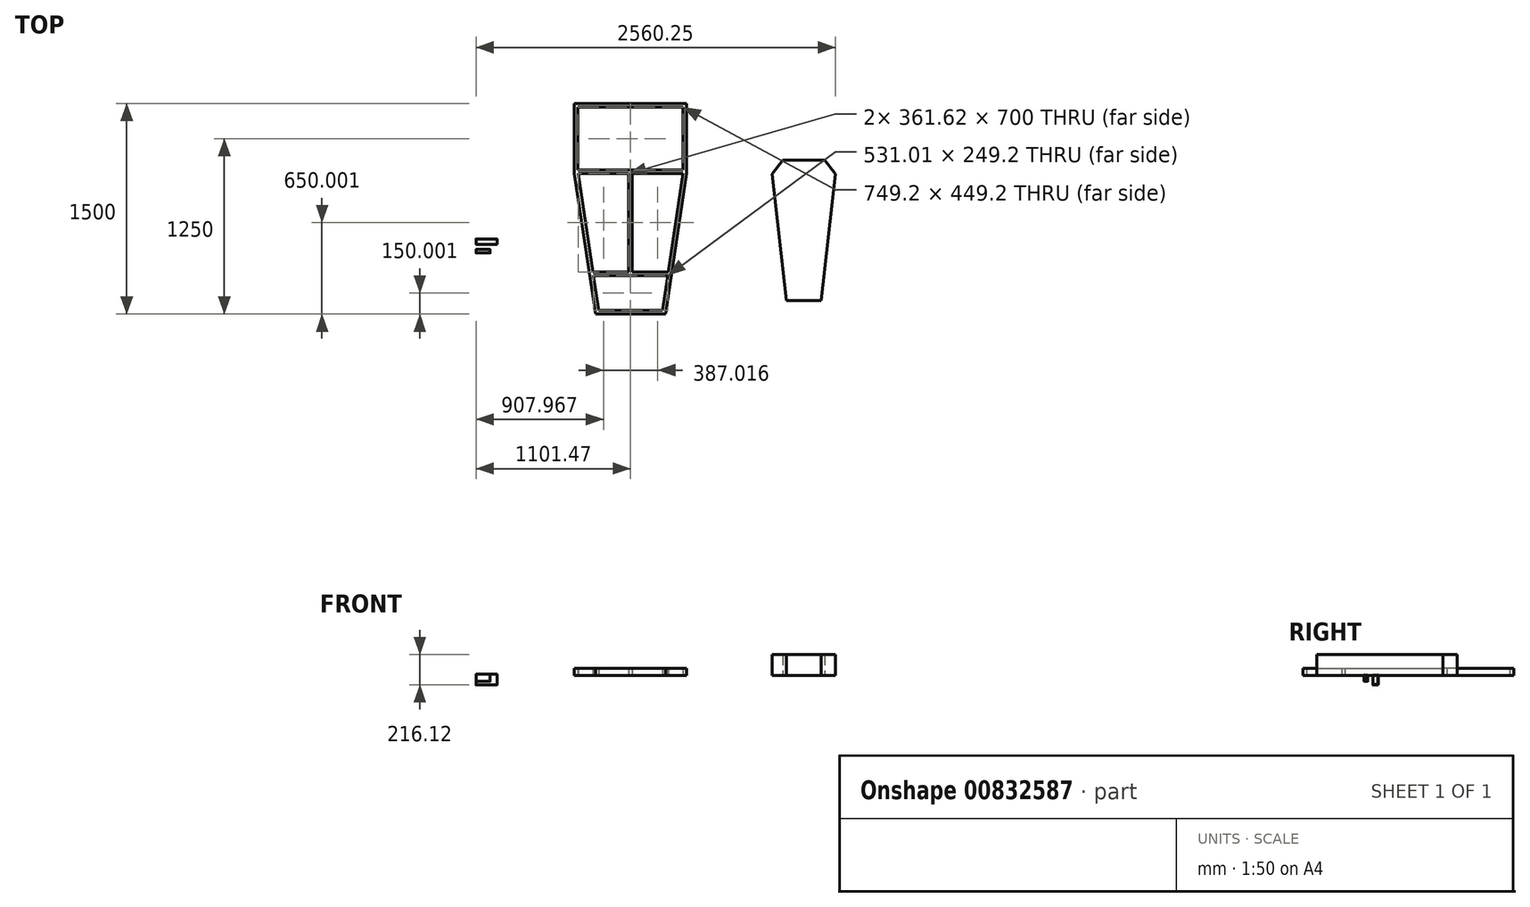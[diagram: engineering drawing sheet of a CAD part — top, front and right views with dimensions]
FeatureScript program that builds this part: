
annotation { "Feature Type Name" : "Feature", "Feature Type Description" : "" }
export const myFeature = defineFeature(function(context is Context, id is Id, definition is map)
    precondition{}
    {
        {
            var Q0;
            Q0=qCreatedBy(makeId("Right.planeOp"),FACE);
            var sketch = newSketch(context, id + "F0", { "sketchPlane" : qUnion([Q0])});
            skLineSegment(sketch, "E0.bottom", {"start": v(-5.09, 9.16) * mm, "end": v(18.31, 9.16) * mm});
            skLineSegment(sketch, "E0.top", {"start": v(-5.09, -41.64) * mm, "end": v(18.31, -41.64) * mm});
            skLineSegment(sketch, "E0.left", {"start": v(-6.09, 8.16) * mm, "end": v(-6.09, -40.64) * mm});
            skLineSegment(sketch, "E0.right", {"start": v(19.31, 8.16) * mm, "end": v(19.31, -40.64) * mm});
            skPoint(sketch, "E1.visualSharp", {"position": v(-6.09, 9.16) * mm});
            skArc(sketch, "E1.filletArc", {"start": v(-5.09, 9.16) * mm, "mid": v(-5.8, 8.87) * mm, "end": v(-6.09, 8.16) * mm});
            skPoint(sketch, "E2.visualSharp", {"position": v(19.31, 9.16) * mm});
            skArc(sketch, "E2.filletArc", {"start": v(19.31, 8.16) * mm, "mid": v(19.02, 8.87) * mm, "end": v(18.31, 9.16) * mm});
            skPoint(sketch, "E3.visualSharp", {"position": v(19.31, -41.64) * mm});
            skArc(sketch, "E3.filletArc", {"start": v(18.31, -41.64) * mm, "mid": v(19.02, -41.34) * mm, "end": v(19.31, -40.64) * mm});
            skPoint(sketch, "E4.visualSharp", {"position": v(-6.09, -41.64) * mm});
            skArc(sketch, "E4.filletArc", {"start": v(-6.09, -40.64) * mm, "mid": v(-5.8, -41.34) * mm, "end": v(-5.09, -41.64) * mm});
            skLineSegment(sketch, "E5.0", {"start": v(-2.98, 7.06) * mm, "end": v(16.2, 7.06) * mm});
            skLineSegment(sketch, "E5.1", {"start": v(-3.98, 6.06) * mm, "end": v(-3.98, -38.53) * mm});
            skLineSegment(sketch, "E5.2", {"start": v(-2.98, -39.53) * mm, "end": v(16.2, -39.53) * mm});
            skLineSegment(sketch, "E5.3", {"start": v(17.2, 6.06) * mm, "end": v(17.2, -38.53) * mm});
            skPoint(sketch, "E6.visualSharp", {"position": v(-3.98, 7.06) * mm});
            skArc(sketch, "E6.filletArc", {"start": v(-2.98, 7.06) * mm, "mid": v(-3.69, 6.76) * mm, "end": v(-3.98, 6.06) * mm});
            skPoint(sketch, "E7.visualSharp", {"position": v(17.2, 7.06) * mm});
            skArc(sketch, "E7.filletArc", {"start": v(17.2, 6.06) * mm, "mid": v(16.91, 6.76) * mm, "end": v(16.2, 7.06) * mm});
            skPoint(sketch, "E8.visualSharp", {"position": v(-3.98, -39.53) * mm});
            skArc(sketch, "E8.filletArc", {"start": v(-3.98, -38.53) * mm, "mid": v(-3.69, -39.24) * mm, "end": v(-2.98, -39.53) * mm});
            skPoint(sketch, "E9.visualSharp", {"position": v(17.2, -39.53) * mm});
            skArc(sketch, "E9.filletArc", {"start": v(16.2, -39.53) * mm, "mid": v(16.91, -39.24) * mm, "end": v(17.2, -38.53) * mm});
            skLineSegment(sketch, "E10.bottom", {"start": v(56.7, 10.08) * mm, "end": v(92.8, 10.08) * mm});
            skLineSegment(sketch, "E10.top", {"start": v(56.7, -66.12) * mm, "end": v(92.8, -66.12) * mm});
            skLineSegment(sketch, "E10.left", {"start": v(55.7, 9.08) * mm, "end": v(55.7, -65.12) * mm});
            skLineSegment(sketch, "E10.right", {"start": v(93.8, 9.08) * mm, "end": v(93.8, -65.12) * mm});
            skLineSegment(sketch, "E11.0", {"start": v(57.81, 6.97) * mm, "end": v(57.81, -63.01) * mm});
            skLineSegment(sketch, "E11.1", {"start": v(58.81, 7.97) * mm, "end": v(90.7, 7.97) * mm});
            skLineSegment(sketch, "E11.2", {"start": v(91.7, 6.97) * mm, "end": v(91.7, -63.01) * mm});
            skLineSegment(sketch, "E11.3", {"start": v(58.81, -64.01) * mm, "end": v(90.7, -64.01) * mm});
            skPoint(sketch, "E12.visualSharp", {"position": v(55.7, 10.08) * mm});
            skArc(sketch, "E12.filletArc", {"start": v(56.7, 10.08) * mm, "mid": v(56, 9.79) * mm, "end": v(55.7, 9.08) * mm});
            skPoint(sketch, "E13.visualSharp", {"position": v(57.81, 7.97) * mm});
            skArc(sketch, "E13.filletArc", {"start": v(58.81, 7.97) * mm, "mid": v(58.1, 7.68) * mm, "end": v(57.81, 6.97) * mm});
            skPoint(sketch, "E14.visualSharp", {"position": v(91.7, 7.97) * mm});
            skArc(sketch, "E14.filletArc", {"start": v(91.7, 6.97) * mm, "mid": v(91.4, 7.68) * mm, "end": v(90.7, 7.97) * mm});
            skPoint(sketch, "E15.visualSharp", {"position": v(93.8, 10.08) * mm});
            skArc(sketch, "E15.filletArc", {"start": v(93.8, 9.08) * mm, "mid": v(93.51, 9.79) * mm, "end": v(92.8, 10.08) * mm});
            skPoint(sketch, "E16.visualSharp", {"position": v(91.7, -64.01) * mm});
            skArc(sketch, "E16.filletArc", {"start": v(90.7, -64.01) * mm, "mid": v(91.4, -63.72) * mm, "end": v(91.7, -63.01) * mm});
            skPoint(sketch, "E17.visualSharp", {"position": v(93.8, -66.12) * mm});
            skArc(sketch, "E17.filletArc", {"start": v(92.8, -66.12) * mm, "mid": v(93.51, -65.83) * mm, "end": v(93.8, -65.12) * mm});
            skPoint(sketch, "E18.visualSharp", {"position": v(55.7, -66.12) * mm});
            skArc(sketch, "E18.filletArc", {"start": v(55.7, -65.12) * mm, "mid": v(56, -65.83) * mm, "end": v(56.7, -66.12) * mm});
            skPoint(sketch, "E19.visualSharp", {"position": v(57.81, -64.01) * mm});
            skArc(sketch, "E19.filletArc", {"start": v(57.81, -63.01) * mm, "mid": v(58.1, -63.72) * mm, "end": v(58.81, -64.01) * mm});
            skSolve(sketch);
        }
        {
            var Q0;
            Q0=makeQuery(id+"F0.imprint","IMPRINT",FACE,{"disambiguationData":[TD([[makeQuery(id+"F0.imprint","IMPRINT",EDGE,{"derivedFrom":sQuery(id+"F0.wireOp",EDGE,"E0.bottom")}),-1.0]])]});
            extrude(context, id + "F1", {"entities" : qUnion([Q0]), "depth" : 100 * mm, "offsetDistance" : 25 * mm});
        }
        {
            var Q0;
            Q0=makeQuery(id+"F0.imprint","IMPRINT",FACE,{"disambiguationData":[TD([[makeQuery(id+"F0.imprint","IMPRINT",EDGE,{"derivedFrom":sQuery(id+"F0.wireOp",EDGE,"E10.bottom")}),-1.0]])]});
            extrude(context, id + "F2", {"entities" : qUnion([Q0]), "depth" : 150 * mm, "offsetDistance" : 25 * mm});
        }
        {
            var Q0;
            Q0=qCreatedBy(makeId("Top.planeOp"),FACE);
            var sketch = newSketch(context, id + "F3", { "sketchPlane" : qUnion([Q0])});
            skLineSegment(sketch, "E20.left", {"start": v(701.47, 1058.38) * mm, "end": v(701.47, 558.38) * mm});
            skLineSegment(sketch, "E20.right", {"start": v(1501.47, 1058.38) * mm, "end": v(1501.47, 558.38) * mm});
            skLineSegment(sketch, "E21", {"start": v(701.47, 1058.38) * mm, "end": v(1501.47, 1058.38) * mm});
            skLineSegment(sketch, "E22", {"start": v(1114.17, 558.38) * mm, "end": v(1475.8, 558.38) * mm});
            skLineSegment(sketch, "E23", {"start": v(1088.77, 558.38) * mm, "end": v(727.16, 558.38) * mm});
            skLineSegment(sketch, "E24", {"start": v(1101.47, -441.62) * mm, "end": v(1351.47, -441.62) * mm});
            skLineSegment(sketch, "E25", {"start": v(1351.47, -441.62) * mm, "end": v(1501.47, 558.38) * mm});
            skLineSegment(sketch, "E26", {"start": v(1101.47, -441.62) * mm, "end": v(851.47, -441.62) * mm});
            skLineSegment(sketch, "E27", {"start": v(851.47, -441.62) * mm, "end": v(701.47, 558.38) * mm});
            skLineSegment(sketch, "E28.0", {"start": v(726.87, 1032.98) * mm, "end": v(726.87, 583.78) * mm});
            skLineSegment(sketch, "E28.1", {"start": v(873.35, -416.22) * mm, "end": v(835.97, -167.02) * mm});
            skLineSegment(sketch, "E28.2", {"start": v(1476.07, 1032.98) * mm, "end": v(1476.07, 583.78) * mm});
            skLineSegment(sketch, "E28.3", {"start": v(1329.6, -416.22) * mm, "end": v(1366.98, -167.02) * mm});
            skLineSegment(sketch, "E28.4", {"start": v(1101.47, -416.22) * mm, "end": v(1329.6, -416.22) * mm});
            skLineSegment(sketch, "E28.5", {"start": v(726.87, 1032.98) * mm, "end": v(1476.07, 1032.98) * mm});
            skLineSegment(sketch, "E28.6", {"start": v(1101.47, -416.22) * mm, "end": v(873.35, -416.22) * mm});
            skLineSegment(sketch, "E29.0", {"start": v(1101.47, 583.78) * mm, "end": v(726.87, 583.78) * mm});
            skLineSegment(sketch, "E29.1", {"start": v(1101.47, 583.78) * mm, "end": v(1476.07, 583.78) * mm});
            skLineSegment(sketch, "E30", {"start": v(1088.77, -141.62) * mm, "end": v(832.16, -141.62) * mm});
            skLineSegment(sketch, "E31", {"start": v(1114.17, -141.62) * mm, "end": v(1370.8, -141.62) * mm});
            skLineSegment(sketch, "E32.0", {"start": v(1114.17, -141.62) * mm, "end": v(1114.17, 558.38) * mm});
            skLineSegment(sketch, "E33.0", {"start": v(1088.77, -141.62) * mm, "end": v(1088.77, 558.38) * mm});
            skLineSegment(sketch, "E34.0", {"start": v(1101.47, -167.02) * mm, "end": v(835.97, -167.02) * mm});
            skLineSegment(sketch, "E34.1", {"start": v(1101.47, -167.02) * mm, "end": v(1366.98, -167.02) * mm});
            skLineSegment(sketch, "E35.trimOffspring", {"start": v(1370.8, -141.62) * mm, "end": v(1476.07, 560.28) * mm});
            skLineSegment(sketch, "E36.trimOffspring", {"start": v(832.16, -141.62) * mm, "end": v(726.87, 560.28) * mm});
            skSolve(sketch);
        }
        {
            var Q0;
            Q0=qCreatedBy(makeId("Top.planeOp"),FACE);
            var sketch = newSketch(context, id + "F4", { "sketchPlane" : qUnion([Q0])});
            skLineSegment(sketch, "E37", {"start": v(2335.25, -344.21) * mm, "end": v(2210.25, -344.21) * mm});
            skLineSegment(sketch, "E38", {"start": v(2335.25, -344.21) * mm, "end": v(2460.25, -344.21) * mm});
            skLineSegment(sketch, "E39", {"start": v(2560.25, 555.79) * mm, "end": v(2460.25, -344.21) * mm});
            skLineSegment(sketch, "E40", {"start": v(2110.25, 555.79) * mm, "end": v(2210.25, -344.21) * mm});
            skLineSegment(sketch, "E41", {"start": v(2335.25, 655.79) * mm, "end": v(2185.25, 655.79) * mm});
            skLineSegment(sketch, "E42", {"start": v(2185.25, 655.79) * mm, "end": v(2110.25, 555.79) * mm});
            skLineSegment(sketch, "E43", {"start": v(2335.25, 655.79) * mm, "end": v(2485.25, 655.79) * mm});
            skLineSegment(sketch, "E44", {"start": v(2485.25, 655.79) * mm, "end": v(2560.25, 555.79) * mm});
            skSolve(sketch);
        }
        {
            var Q0;
            Q0=makeQuery(id+"F4.imprint","IMPRINT",FACE,{"disambiguationData":[TD([[makeQuery(id+"F4.imprint","IMPRINT",EDGE,{"derivedFrom":sQuery(id+"F4.wireOp",EDGE,"E37")}),-1.0]])]});
            extrude(context, id + "F5", {"entities" : qUnion([Q0]), "depth" : 150 * mm, "offsetDistance" : 25 * mm});
        }
        {
            var Q0;
            Q0=makeQuery(id+"F3.imprint","IMPRINT",FACE,{"disambiguationData":[TD([[makeQuery(id+"F3.imprint","IMPRINT",EDGE,{"derivedFrom":sQuery(id+"F3.wireOp",EDGE,"E20.left")}),1.0]])]});
            extrude(context, id + "F6", {"entities" : qUnion([Q0]), "depth" : 50.8 * mm, "offsetDistance" : 25 * mm});
        }
    });
